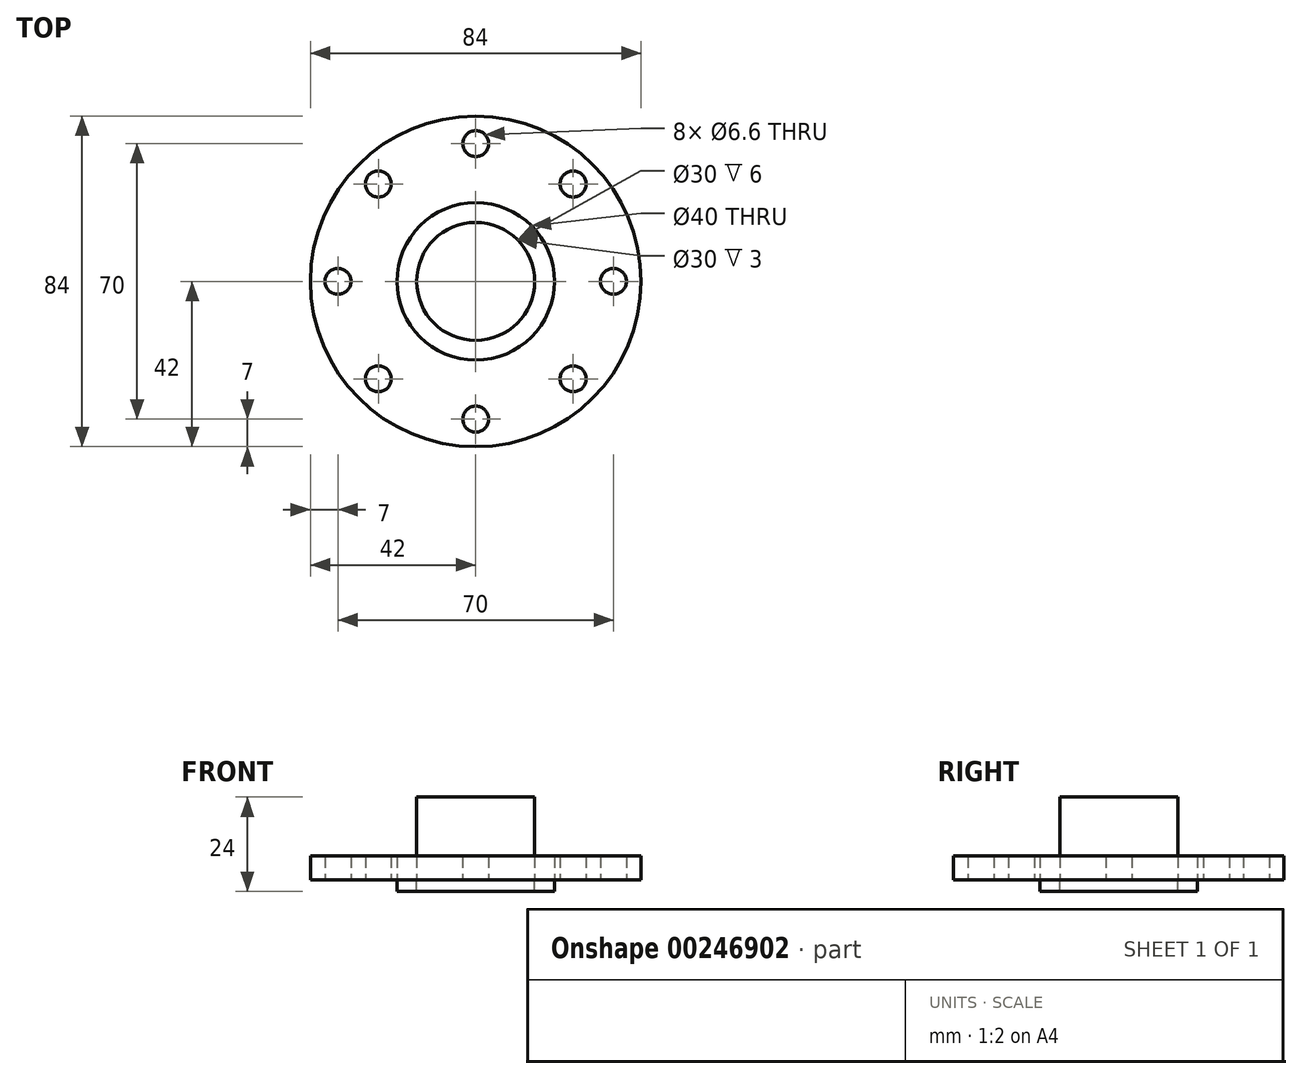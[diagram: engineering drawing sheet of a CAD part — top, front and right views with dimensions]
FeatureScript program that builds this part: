
annotation { "Feature Type Name" : "Feature", "Feature Type Description" : "" }
export const myFeature = defineFeature(function(context is Context, id is Id, definition is map)
    precondition{}
    {
        {
            var Q0;
            Q0=qCreatedBy(makeId("Top.planeOp"),FACE);
            var sketch = newSketch(context, id + "F0", { "sketchPlane" : qUnion([Q0])});
            skCircle(sketch, "E0", {"center": v(0, 0) * mm, "radius": 42 * mm});
            skCircle(sketch, "E1", {"center": v(0, 0) * mm, "radius": 20 * mm});
            skCircle(sketch, "E2", {"center": v(0, 0) * mm, "radius": 15 * mm});
            skCircle(sketch, "E3", {"center": v(0, 35) * mm, "radius": 3.3 * mm});
            skCircle(sketch, "E4.1.0", {"center": v(-24.75, 24.75) * mm, "radius": 3.3 * mm});
            skCircle(sketch, "E4.2.0", {"center": v(-35, 0) * mm, "radius": 3.3 * mm});
            skCircle(sketch, "E4.3.0", {"center": v(-24.75, -24.75) * mm, "radius": 3.3 * mm});
            skCircle(sketch, "E4.4.0", {"center": v(0, -35) * mm, "radius": 3.3 * mm});
            skCircle(sketch, "E4.5.0", {"center": v(24.75, -24.75) * mm, "radius": 3.3 * mm});
            skCircle(sketch, "E4.6.0", {"center": v(35, 0) * mm, "radius": 3.3 * mm});
            skCircle(sketch, "E4.7.0", {"center": v(24.75, 24.75) * mm, "radius": 3.3 * mm});
            skSolve(sketch);
        }
        {
            var Q0;
            Q0=makeQuery(id+"F0.imprint","IMPRINT",FACE,{"disambiguationData":[TD([[makeQuery(id+"F0.imprint","IMPRINT",EDGE,{"derivedFrom":sQuery(id+"F0.wireOp",EDGE,"E1")}),1.0]])]});
            extrude(context, id + "F1", {"entities" : qUnion([Q0]), "oppositeDirection" : true, "depth" : 3 * mm});
        }
        {
            var Q0;
            Q0=makeQuery(id+"F0.imprint","IMPRINT",FACE,{"disambiguationData":[TD([[makeQuery(id+"F0.imprint","IMPRINT",EDGE,{"derivedFrom":sQuery(id+"F0.wireOp",EDGE,"E2")}),1.0]])]});
            extrude(context, id + "F2", {"entities" : qUnion([Q0]), "depth" : 21 * mm});
        }
        {
            var Q0;
            Q0=makeQuery(id+"F0.imprint","IMPRINT",FACE,{"disambiguationData":[TD([[makeQuery(id+"F0.imprint","IMPRINT",EDGE,{"derivedFrom":sQuery(id+"F0.wireOp",EDGE,"E0")}),1.0]])]});
            extrude(context, id + "F3", {"entities" : qUnion([Q0]), "depth" : 6 * mm});
        }
        {
            var Q0;
            Q0=makeQuery(id+"F0.imprint","IMPRINT",FACE,{"disambiguationData":[TD([[makeQuery(id+"F0.imprint","IMPRINT",EDGE,{"derivedFrom":sQuery(id+"F0.wireOp",EDGE,"E1")}),1.0]])]});
            extrude(context, id + "F4", {"entities" : qUnion([Q0]), "depth" : 6 * mm});
        }
    });
